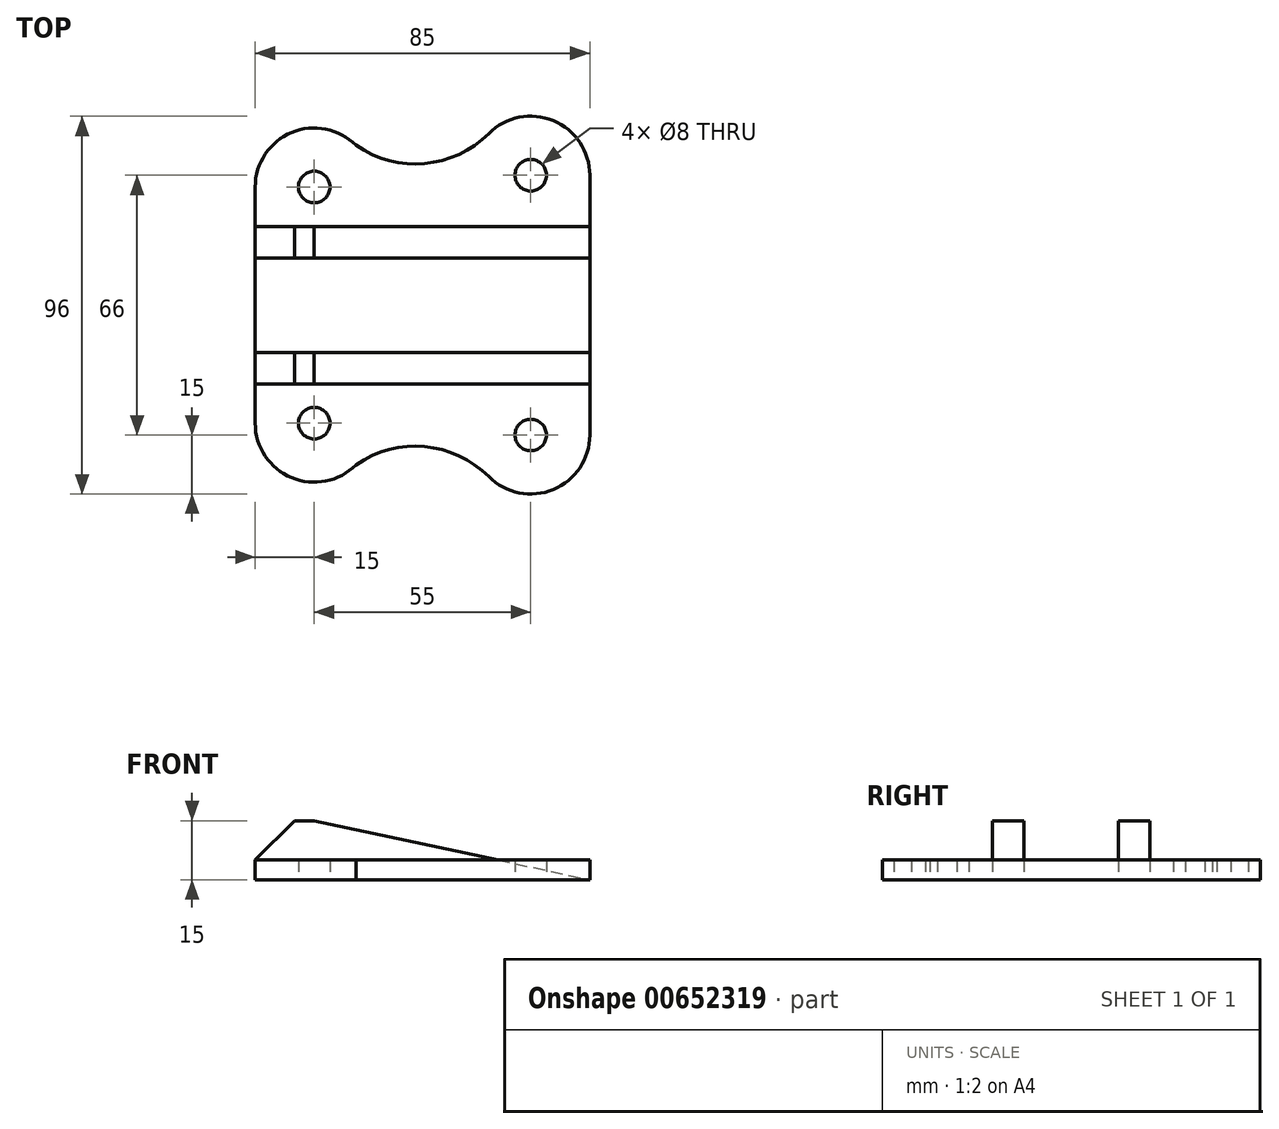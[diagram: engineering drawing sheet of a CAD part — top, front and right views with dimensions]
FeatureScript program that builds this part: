
annotation { "Feature Type Name" : "Feature", "Feature Type Description" : "" }
export const myFeature = defineFeature(function(context is Context, id is Id, definition is map)
    precondition{}
    {
        {
            var Q0;
            Q0=qCreatedBy(makeId("Top.planeOp"),FACE);
            var sketch = newSketch(context, id + "F0", { "sketchPlane" : qUnion([Q0])});
            skCircle(sketch, "E0", {"center": v(-30, 30) * mm, "radius": 15 * mm});
            skCircle(sketch, "E1", {"center": v(-30, -30) * mm, "radius": 15 * mm});
            skCircle(sketch, "E2", {"center": v(25, 33) * mm, "radius": 15 * mm});
            skCircle(sketch, "E3", {"center": v(25, -33) * mm, "radius": 15 * mm});
            skLineSegment(sketch, "E4", {"start": v(-30, 30) * mm, "end": v(-19.4, 40.6) * mm});
            skLineSegment(sketch, "E5", {"start": v(25, 33) * mm, "end": v(14.4, 43.6) * mm});
            skArc(sketch, "E6", {"start": v(-19.4, 40.6) * mm, "mid": v(-1.96, 35.97) * mm, "end": v(14.4, 43.6) * mm});
            skLineSegment(sketch, "E7", {"start": v(-30, -30) * mm, "end": v(-19.4, -40.6) * mm});
            skLineSegment(sketch, "E8", {"start": v(25, -33) * mm, "end": v(14.4, -43.6) * mm});
            skArc(sketch, "E9", {"start": v(14.4, -43.6) * mm, "mid": v(-1.96, -35.97) * mm, "end": v(-19.4, -40.6) * mm});
            skLineSegment(sketch, "E10", {"start": v(-45, 30) * mm, "end": v(-45, -30) * mm});
            skLineSegment(sketch, "E11", {"start": v(40, 33) * mm, "end": v(40, -33) * mm});
            skSolve(sketch);
        }
        {
            var Q0;
            {var subQ0=sQuery(id+"F0.wireOp",EDGE,"E6");Q0=makeQuery(id+"F0.imprint","IMPRINT",FACE,{"disambiguationData":[TD([[makeQuery(id+"F0.imprint","IMPRINT",EDGE,{"derivedFrom":subQ0}),-1.0]])]});}
            var Q1;
            {var subQ0=sQuery(id+"F0.wireOp",EDGE,"E1");var subQ1=makeQuery(id+"F0.imprint","INTERSECT",VERTEX,{"derivedFrom":[subQ0,sQuery(id+"F0.wireOp",EDGE,"E9")]});Q1=makeQuery(id+"F0.imprint","IMPRINT",FACE,{"disambiguationData":[TD([[makeQuery(id+"F0.imprint","IMPRINT",EDGE,{"disambiguationData":[TD([[subQ1,1.0]])],"derivedFrom":subQ0}),1.0]])]});}
            var Q2;
            {var subQ0=sQuery(id+"F0.wireOp",EDGE,"E0");var subQ1=makeQuery(id+"F0.imprint","INTERSECT",VERTEX,{"derivedFrom":[subQ0,sQuery(id+"F0.wireOp",EDGE,"E6")]});Q2=makeQuery(id+"F0.imprint","IMPRINT",FACE,{"disambiguationData":[TD([[makeQuery(id+"F0.imprint","IMPRINT",EDGE,{"disambiguationData":[TD([[subQ1,-1.0]])],"derivedFrom":subQ0}),1.0]])]});}
            var Q3;
            {var subQ0=sQuery(id+"F0.wireOp",EDGE,"E2");var subQ1=makeQuery(id+"F0.imprint","INTERSECT",VERTEX,{"derivedFrom":[subQ0,sQuery(id+"F0.wireOp",EDGE,"E6")]});Q3=makeQuery(id+"F0.imprint","IMPRINT",FACE,{"disambiguationData":[TD([[makeQuery(id+"F0.imprint","IMPRINT",EDGE,{"disambiguationData":[TD([[subQ1,1.0]])],"derivedFrom":subQ0}),1.0]])]});}
            var Q4;
            {var subQ0=sQuery(id+"F0.wireOp",EDGE,"E3");var subQ1=makeQuery(id+"F0.imprint","INTERSECT",VERTEX,{"derivedFrom":[subQ0,sQuery(id+"F0.wireOp",EDGE,"E9")]});Q4=makeQuery(id+"F0.imprint","IMPRINT",FACE,{"disambiguationData":[TD([[makeQuery(id+"F0.imprint","IMPRINT",EDGE,{"disambiguationData":[TD([[subQ1,1.0]])],"derivedFrom":subQ0}),1.0]])]});}
            extrude(context, id + "F1", {"entities" : qUnion([Q0, Q1, Q2, Q3, Q4]), "depth" : 5 * mm, "offsetDistance" : 25 * mm});
        }
        {
            var Q0;
            Q0=qCreatedBy(makeId("Top.planeOp"),FACE);
            var sketch = newSketch(context, id + "F2", { "sketchPlane" : qUnion([Q0])});
            skCircle(sketch, "E12", {"center": v(-30, 30) * mm, "radius": 4 * mm});
            skCircle(sketch, "E13", {"center": v(25, 33) * mm, "radius": 4 * mm});
            skCircle(sketch, "E14", {"center": v(25, -33) * mm, "radius": 4 * mm});
            skCircle(sketch, "E15", {"center": v(-30, -30) * mm, "radius": 4 * mm});
            skSolve(sketch);
        }
        {
            var Q0;
            Q0=makeQuery(id+"F2.imprint","IMPRINT",FACE,{"disambiguationData":[TD([[makeQuery(id+"F2.imprint","IMPRINT",EDGE,{"derivedFrom":sQuery(id+"F2.wireOp",EDGE,"E12")}),1.0]])]});
            var Q1;
            Q1=makeQuery(id+"F2.imprint","IMPRINT",FACE,{"disambiguationData":[TD([[makeQuery(id+"F2.imprint","IMPRINT",EDGE,{"derivedFrom":sQuery(id+"F2.wireOp",EDGE,"E13")}),1.0]])]});
            var Q2;
            Q2=makeQuery(id+"F2.imprint","IMPRINT",FACE,{"disambiguationData":[TD([[makeQuery(id+"F2.imprint","IMPRINT",EDGE,{"derivedFrom":sQuery(id+"F2.wireOp",EDGE,"E14")}),1.0]])]});
            var Q3;
            Q3=makeQuery(id+"F2.imprint","IMPRINT",FACE,{"disambiguationData":[TD([[makeQuery(id+"F2.imprint","IMPRINT",EDGE,{"derivedFrom":sQuery(id+"F2.wireOp",EDGE,"E15")}),1.0]])]});
            var Q4;
            Q4 = qSketchRegion(id + "F5", true);
            extrude(context, id + "F3", {"entities" : qUnion([Q0, Q1, Q2, Q3, Q4]), "depth" : 25 * mm, "offsetDistance" : 25 * mm});
        }
        {
            var Q0;
            Q0=makeQuery(id+"F3.opExtrude","SWEPT_BODY",BODY,{"disambiguationData":[OSD([sQuery(id+"F2.wireOp",EDGE,"E12")])]});
            var Q1;
            Q1=makeQuery(id+"F3.opExtrude","SWEPT_BODY",BODY,{"disambiguationData":[OSD([sQuery(id+"F2.wireOp",EDGE,"E13")])]});
            var Q2;
            Q2=makeQuery(id+"F3.opExtrude","SWEPT_BODY",BODY,{"disambiguationData":[OSD([sQuery(id+"F2.wireOp",EDGE,"E14")])]});
            var Q3;
            Q3=makeQuery(id+"F3.opExtrude","SWEPT_BODY",BODY,{"disambiguationData":[OSD([sQuery(id+"F2.wireOp",EDGE,"E15")])]});
            var Q4;
            Q4=makeQuery(id+"F1.opExtrude","SWEPT_BODY",BODY,{"disambiguationData":[OSD([sQuery(id+"F0.wireOp",EDGE,"E0"),sQuery(id+"F0.wireOp",EDGE,"E1"),sQuery(id+"F0.wireOp",EDGE,"E2"),sQuery(id+"F0.wireOp",EDGE,"E3"),sQuery(id+"F0.wireOp",EDGE,"E6"),sQuery(id+"F0.wireOp",EDGE,"E9"),sQuery(id+"F0.wireOp",EDGE,"E10"),sQuery(id+"F0.wireOp",EDGE,"E11")])]});
            booleanBodies(context, id + "F4", {"operationType" : BooleanOperationType.SUBTRACTION, "tools" : qUnion([Q0, Q1, Q2, Q3]), "targets" : qUnion([Q4])});
        }
        {
            var Q0;
            Q0=qCreatedBy(makeId("Top.planeOp"),FACE);
            var sketch = newSketch(context, id + "F5", { "sketchPlane" : qUnion([Q0])});
            skLineSegment(sketch, "E16.bottom", {"start": v(-45, 20) * mm, "end": v(40, 20) * mm});
            skLineSegment(sketch, "E16.top", {"start": v(-45, 12) * mm, "end": v(40, 12) * mm});
            skLineSegment(sketch, "E16.left", {"start": v(-45, 20) * mm, "end": v(-45, 12) * mm});
            skLineSegment(sketch, "E16.right", {"start": v(40, 20) * mm, "end": v(40, 12) * mm});
            skLineSegment(sketch, "E17.bottom", {"start": v(-45, -12) * mm, "end": v(40, -12) * mm});
            skLineSegment(sketch, "E17.top", {"start": v(-45, -20) * mm, "end": v(40, -20) * mm});
            skLineSegment(sketch, "E17.left", {"start": v(-45, -12) * mm, "end": v(-45, -20) * mm});
            skLineSegment(sketch, "E17.right", {"start": v(40, -12) * mm, "end": v(40, -20) * mm});
            skSolve(sketch);
        }
        {
            var Q0;
            Q0=makeQuery(id+"F5.imprint","IMPRINT",FACE,{"disambiguationData":[TD([[makeQuery(id+"F5.imprint","IMPRINT",EDGE,{"derivedFrom":sQuery(id+"F5.wireOp",EDGE,"E16.bottom")}),-1.0]])]});
            var Q1;
            Q1=makeQuery(id+"F5.imprint","IMPRINT",FACE,{"disambiguationData":[TD([[makeQuery(id+"F5.imprint","IMPRINT",EDGE,{"derivedFrom":sQuery(id+"F5.wireOp",EDGE,"E17.bottom")}),-1.0]])]});
            extrude(context, id + "F6", {"entities" : qUnion([Q0, Q1]), "depth" : 15 * mm, "offsetDistance" : 25 * mm});
        }
        {
            var Q0;
            Q0=makeQuery(id+"F6.opExtrude","CAP_EDGE",EDGE,{"disambiguationData":[OSD([sQuery(id+"F5.wireOp",EDGE,"E16.right")])],"isStart":false});
            var Q1;
            Q1=makeQuery(id+"F6.opExtrude","CAP_EDGE",EDGE,{"disambiguationData":[OSD([sQuery(id+"F5.wireOp",EDGE,"E17.right")])],"isStart":false});
            chamfer(context, id + "F7", {"entities" : qUnion([Q0, Q1]), "chamferType" : ChamferType.TWO_OFFSETS, "width1" : 15 * mm, "oppositeDirection" : false, "width2" : 70 * mm, "tangentPropagation" : true});
        }
        {
            var Q0;
            Q0=makeQuery(id+"F6.opExtrude","CAP_EDGE",EDGE,{"disambiguationData":[OSD([sQuery(id+"F5.wireOp",EDGE,"E16.left")])],"isStart":false});
            var Q1;
            Q1=makeQuery(id+"F6.opExtrude","CAP_EDGE",EDGE,{"disambiguationData":[OSD([sQuery(id+"F5.wireOp",EDGE,"E17.left")])],"isStart":false});
            chamfer(context, id + "F8", {"entities" : qUnion([Q0, Q1]), "width" : 10 * mm, "tangentPropagation" : true});
        }
    });
